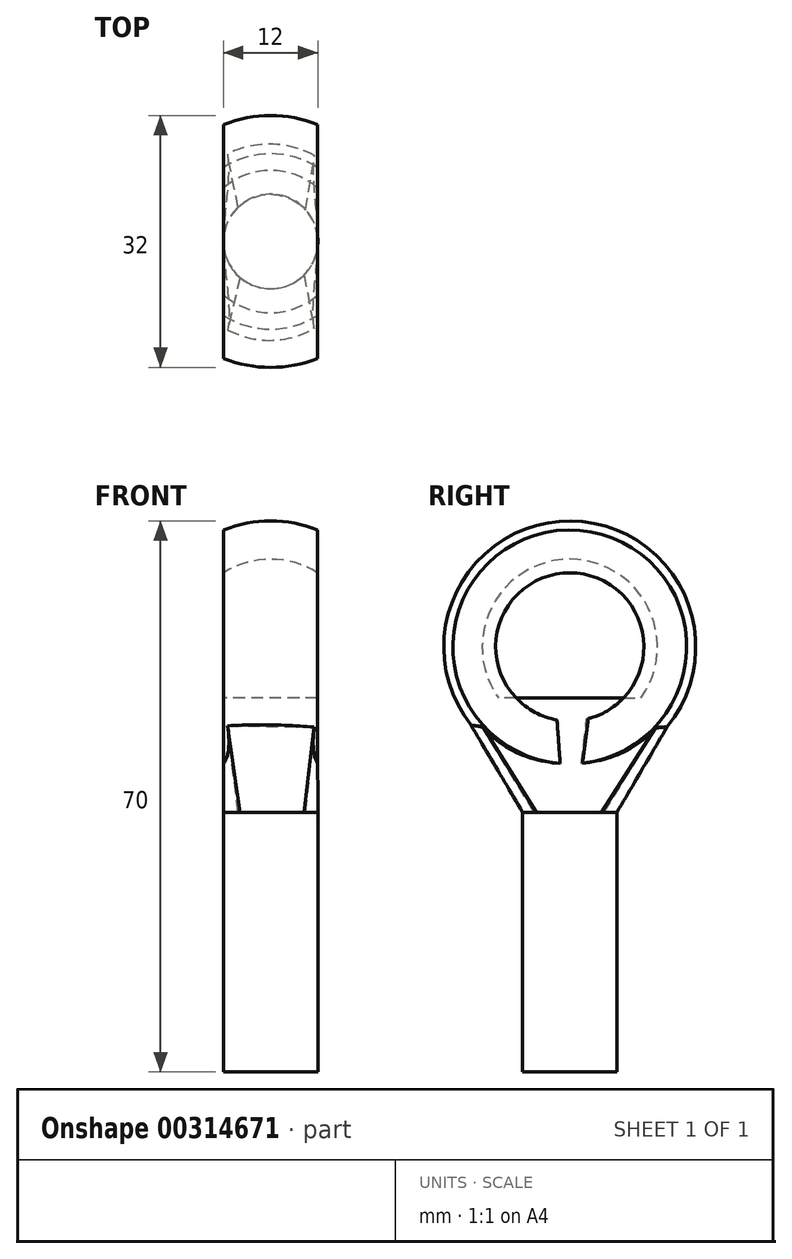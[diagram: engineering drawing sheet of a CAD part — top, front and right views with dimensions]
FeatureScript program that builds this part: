
annotation { "Feature Type Name" : "Feature", "Feature Type Description" : "" }
export const myFeature = defineFeature(function(context is Context, id is Id, definition is map)
    precondition{}
    {
        {
            var Q0;
            Q0=qCreatedBy(makeId("Front.planeOp"),FACE);
            var sketch = newSketch(context, id + "F0", { "sketchPlane" : qUnion([Q0])});
            skLineSegment(sketch, "E0", {"start": v(-35.04, 0) * mm, "end": v(30.48, 0) * mm, "construction": true});
            skArc(sketch, "E1", {"start": v(5.95, 14.85) * mm, "mid": v(0, 16) * mm, "end": v(-5.95, 14.85) * mm});
            skArc(sketch, "E2.trimOffspring", {"start": v(5.95, 9.41) * mm, "mid": v(0, 11.14) * mm, "end": v(-5.95, 9.41) * mm});
            skLineSegment(sketch, "E3", {"start": v(-5.95, 9.41) * mm, "end": v(-5.95, 14.85) * mm});
            skLineSegment(sketch, "E4", {"start": v(5.95, 9.41) * mm, "end": v(5.95, 14.85) * mm});
            skLineSegment(sketch, "E5", {"start": v(-5.95, 12.13) * mm, "end": v(5.95, 12.13) * mm});
            skLineSegment(sketch, "E6", {"start": v(0, 16) * mm, "end": v(0, 11.14) * mm, "construction": true});
            skSolve(sketch);
        }
        {
            var Q0;
            {var subQ5=sQuery(id+"F0.wireOp",EDGE,"E5");Q0=makeQuery(id+"F0.imprint","IMPRINT",FACE,{"disambiguationData":[TD([[makeQuery(id+"F0.imprint","IMPRINT",EDGE,{"derivedFrom":subQ5}),1.0]])]});}
            var Q1;
            {var subQ5=sQuery(id+"F0.wireOp",EDGE,"E5");Q1=makeQuery(id+"F0.imprint","IMPRINT",FACE,{"disambiguationData":[TD([[makeQuery(id+"F0.imprint","IMPRINT",EDGE,{"derivedFrom":subQ5}),-1.0]])]});}
            var Q2;
            Q2=makeQuery(id+"F0.imprint","IMPRINT",FACE,{"disambiguationData":[TD([[makeQuery(id+"F0.imprint","IMPRINT",EDGE,{"derivedFrom":sQuery(id+"F0.wireOp",EDGE,"bZe9K5w0-ARnO-PitD-hnSf-ueX0wNjWXu6K")}),1.0]])]});
            var Q3;
            Q3=sQuery(id+"F0.wireOp",EDGE,"E0");
            revolve(context, id + "F1", {"entities" : qUnion([Q0, Q1, Q2]), "axis" : qUnion([Q3]), "revolveType" : RevolveType.FULL});
        }
        {
            var Q0;
            Q0=qCreatedBy(makeId("Top.planeOp"),FACE);
            cPlane(context, id + "F2", {"entities" : qUnion([Q0]), "cplaneType" : CPlaneType.OFFSET, "offset" : 54 * mm, "oppositeDirection" : true, "width" : 150 * mm, "height" : 150 * mm});
        }
        {
            var Q0;
            Q0=qCreatedBy(id+"F2.planeOp",FACE);
            var sketch = newSketch(context, id + "F3", { "sketchPlane" : qUnion([Q0])});
            skCircle(sketch, "E7", {"center": v(0, 0) * mm, "radius": 6 * mm});
            skSolve(sketch);
        }
        {
            var Q0;
            Q0=makeQuery(id+"F3.imprint","IMPRINT",FACE,{"disambiguationData":[TD([[makeQuery(id+"F3.imprint","IMPRINT",EDGE,{"derivedFrom":sQuery(id+"F3.wireOp",EDGE,"E7")}),1.0]])]});
            extrude(context, id + "F4", {"entities" : qUnion([Q0]), "depth" : 33 * mm});
        }
        {
            var Q0;
            Q0=makeQuery(id+"F4.opExtrude","CAP_FACE",FACE,{"disambiguationData":[OSD([sQuery(id+"F3.wireOp",EDGE,"E7")])],"isStart":false});
            var sketch = newSketch(context, id + "F5", { "sketchPlane" : qUnion([Q0])});
            skArc(sketch, "E8", {"start": v(-3.9, -4.56) * mm, "mid": v(0.24, -6) * mm, "end": v(4.25, -4.23) * mm});
            skArc(sketch, "E9", {"start": v(-4.12, 4.36) * mm, "mid": v(-6, -0.15) * mm, "end": v(-3.9, -4.56) * mm});
            skArc(sketch, "E10", {"start": v(4.46, 4.01) * mm, "mid": v(0.24, 6) * mm, "end": v(-4.12, 4.36) * mm});
            skArc(sketch, "E11", {"start": v(4.25, -4.23) * mm, "mid": v(6, -0.15) * mm, "end": v(4.46, 4.01) * mm});
            skSolve(sketch);
        }
        {
            var Q0;
            Q0=makeQuery(id+"F1.opRevolve","SWEPT_FACE",FACE,{"disambiguationData":[OSD([sQuery(id+"F0.wireOp",EDGE,"E4")])]});
            var sketch = newSketch(context, id + "F6", { "sketchPlane" : qUnion([Q0])});
            skArc(sketch, "E12", {"start": v(-13.35, -6.5) * mm, "mid": v(0, 14.85) * mm, "end": v(13.35, -6.5) * mm});
            skArc(sketch, "E13", {"start": v(13.35, -6.5) * mm, "mid": v(0, -14.85) * mm, "end": v(-13.35, -6.5) * mm});
            skLineSegment(sketch, "E14", {"start": v(13.35, -6.5) * mm, "end": v(-23.8, -6.5) * mm, "construction": true});
            skSolve(sketch);
        }
        {
            var Q0;
            Q0=makeQuery(id+"F5.imprint","IMPRINT",FACE,{"disambiguationData":[TD([[makeQuery(id+"F5.imprint","IMPRINT",EDGE,{"derivedFrom":sQuery(id+"F5.wireOp",EDGE,"E8")}),1.0]])]});
            var Q1;
            Q1=sQuery(id+"F6.wireOp",VERTEX,"E13.end");
            cPlane(context, id + "F7", {"entities" : qUnion([Q0, Q1]), "cplaneType" : CPlaneType.PLANE_POINT, "offset" : 25 * mm, "width" : 150 * mm, "height" : 150 * mm});
        }
        {
            var Q0;
            Q0=qCreatedBy(id+"F7.planeOp",FACE);
            var sketch = newSketch(context, id + "F8", { "sketchPlane" : qUnion([Q0])});
            skLineSegment(sketch, "E15", {"start": v(5.95, -13.35) * mm, "end": v(5.95, 13.35) * mm});
            skLineSegment(sketch, "E16", {"start": v(-5.95, -13.35) * mm, "end": v(-5.95, 13.35) * mm});
            skArc(sketch, "E17", {"start": v(-5.95, -13.35) * mm, "mid": v(0, -14.57) * mm, "end": v(5.95, -13.35) * mm});
            skArc(sketch, "E18", {"start": v(5.95, 13.35) * mm, "mid": v(0, 14.5) * mm, "end": v(-5.95, 13.35) * mm});
            skSolve(sketch);
        }
        {
            var Q1;
            Q1=makeQuery(id+"F5.imprint","IMPRINT",FACE,{"disambiguationData":[TD([[makeQuery(id+"F5.imprint","IMPRINT",EDGE,{"derivedFrom":sQuery(id+"F5.wireOp",EDGE,"E8")}),1.0]])]});
            var Q2;
            Q2 = qSketchRegion(id + "F8", true);
            loft(context, id + "F9", {"operationType" : NewBodyOperationType.ADD, "sheetProfilesArray" : [{ "sheetProfileEntities" : qUnion([Q1]) }, { "sheetProfileEntities" : qUnion([Q2]) }]});
        }
    });
